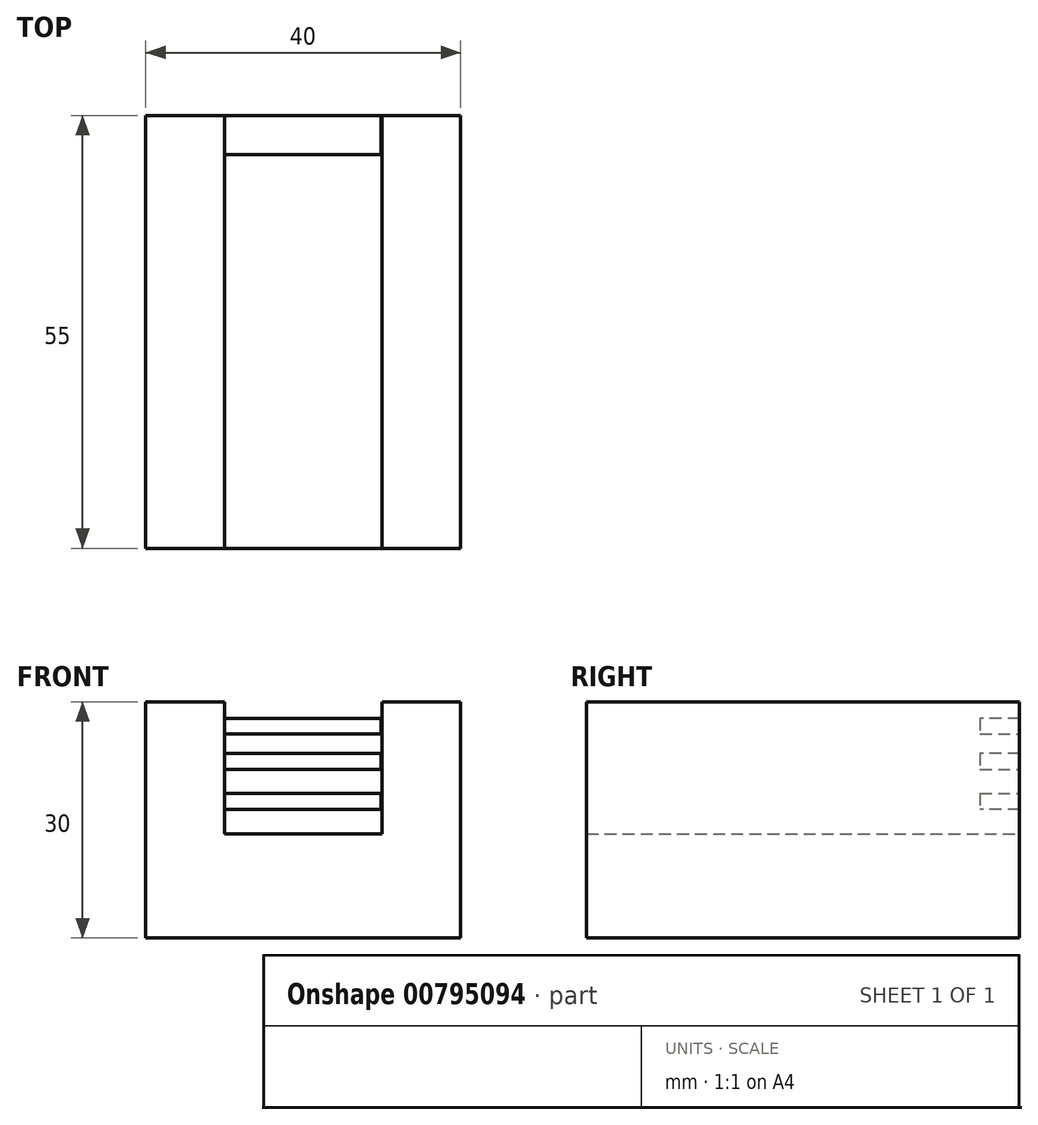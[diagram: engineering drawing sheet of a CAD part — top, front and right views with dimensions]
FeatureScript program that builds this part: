
annotation { "Feature Type Name" : "Feature", "Feature Type Description" : "" }
export const myFeature = defineFeature(function(context is Context, id is Id, definition is map)
    precondition{}
    {
        {
            var Q0;
            Q0=qCreatedBy(makeId("Front.planeOp"),FACE);
            var sketch = newSketch(context, id + "F0", { "sketchPlane" : qUnion([Q0])});
            skLineSegment(sketch, "E0", {"start": v(0, 0) * mm, "end": v(0, 30) * mm});
            skLineSegment(sketch, "E1", {"start": v(0, 30) * mm, "end": v(10, 30) * mm});
            skLineSegment(sketch, "E2", {"start": v(10, 30) * mm, "end": v(10, 13.2) * mm});
            skLineSegment(sketch, "E3", {"start": v(10, 13.2) * mm, "end": v(30, 13.2) * mm});
            skLineSegment(sketch, "E4", {"start": v(30, 13.2) * mm, "end": v(30, 30) * mm});
            skLineSegment(sketch, "E5", {"start": v(30, 30) * mm, "end": v(40, 30) * mm});
            skLineSegment(sketch, "E6", {"start": v(40, 30) * mm, "end": v(40, 0) * mm});
            skLineSegment(sketch, "E7", {"start": v(40, 0) * mm, "end": v(0, 0) * mm});
            skSolve(sketch);
        }
        {
            var Q0;
            Q0=makeQuery(id+"F0.imprint","IMPRINT",FACE,{"disambiguationData":[TD([[makeQuery(id+"F0.imprint","IMPRINT",EDGE,{"derivedFrom":sQuery(id+"F0.wireOp",EDGE,"E0")}),-1.0]])]});
            extrude(context, id + "F1", {"entities" : qUnion([Q0]), "depth" : 50 * mm, "offsetDistance" : 25 * mm});
        }
        {
            var Q0;
            Q0=makeQuery(id+"F1.opExtrude","CAP_FACE",FACE,{"disambiguationData":[OSD([sQuery(id+"F0.wireOp",EDGE,"E0"),sQuery(id+"F0.wireOp",EDGE,"E1"),sQuery(id+"F0.wireOp",EDGE,"E2"),sQuery(id+"F0.wireOp",EDGE,"E3"),sQuery(id+"F0.wireOp",EDGE,"E4"),sQuery(id+"F0.wireOp",EDGE,"E5"),sQuery(id+"F0.wireOp",EDGE,"E6"),sQuery(id+"F0.wireOp",EDGE,"E7")])],"isStart":false});
            extrude(context, id + "F2", {"entities" : qUnion([Q0]), "operationType" : NewBodyOperationType.ADD, "depth" : 5 * mm, "offsetDistance" : 25 * mm});
        }
        {
            var Q0;
            Q0=qCreatedBy(makeId("Front.planeOp"),FACE);
            var sketch = newSketch(context, id + "F3", { "sketchPlane" : qUnion([Q0])});
            skLineSegment(sketch, "E8", {"start": v(9.9, 16.37) * mm, "end": v(29.9, 16.37) * mm});
            skLineSegment(sketch, "E9", {"start": v(29.9, 16.37) * mm, "end": v(29.9, 18.37) * mm});
            skLineSegment(sketch, "E10", {"start": v(29.9, 18.37) * mm, "end": v(9.9, 18.37) * mm});
            skLineSegment(sketch, "E11", {"start": v(9.9, 18.37) * mm, "end": v(9.9, 16.37) * mm});
            skLineSegment(sketch, "E12", {"start": v(9.9, 21.44) * mm, "end": v(9.9, 23.44) * mm});
            skLineSegment(sketch, "E13", {"start": v(9.9, 23.44) * mm, "end": v(29.9, 23.44) * mm});
            skLineSegment(sketch, "E14", {"start": v(29.9, 23.44) * mm, "end": v(29.9, 21.44) * mm});
            skLineSegment(sketch, "E15", {"start": v(29.9, 21.44) * mm, "end": v(9.9, 21.44) * mm});
            skLineSegment(sketch, "E16", {"start": v(9.9, 25.9) * mm, "end": v(9.9, 27.9) * mm});
            skLineSegment(sketch, "E17", {"start": v(9.9, 27.9) * mm, "end": v(29.9, 27.9) * mm});
            skLineSegment(sketch, "E18", {"start": v(29.9, 27.9) * mm, "end": v(29.9, 25.9) * mm});
            skLineSegment(sketch, "E19", {"start": v(29.9, 25.9) * mm, "end": v(9.9, 25.9) * mm});
            skSolve(sketch);
        }
        {
            var Q0;
            Q0=makeQuery(id+"F3.imprint","IMPRINT",FACE,{"disambiguationData":[TD([[makeQuery(id+"F3.imprint","IMPRINT",EDGE,{"derivedFrom":sQuery(id+"F3.wireOp",EDGE,"E8")}),1.0]])]});
            var Q1;
            Q1=makeQuery(id+"F3.imprint","IMPRINT",FACE,{"disambiguationData":[TD([[makeQuery(id+"F3.imprint","IMPRINT",EDGE,{"derivedFrom":sQuery(id+"F3.wireOp",EDGE,"E12")}),-1.0]])]});
            var Q2;
            Q2=makeQuery(id+"F3.imprint","IMPRINT",FACE,{"disambiguationData":[TD([[makeQuery(id+"F3.imprint","IMPRINT",EDGE,{"derivedFrom":sQuery(id+"F3.wireOp",EDGE,"E16")}),-1.0]])]});
            extrude(context, id + "F4", {"entities" : qUnion([Q0, Q1, Q2]), "operationType" : NewBodyOperationType.ADD, "depth" : 5 * mm, "offsetDistance" : 25 * mm});
        }
    });
